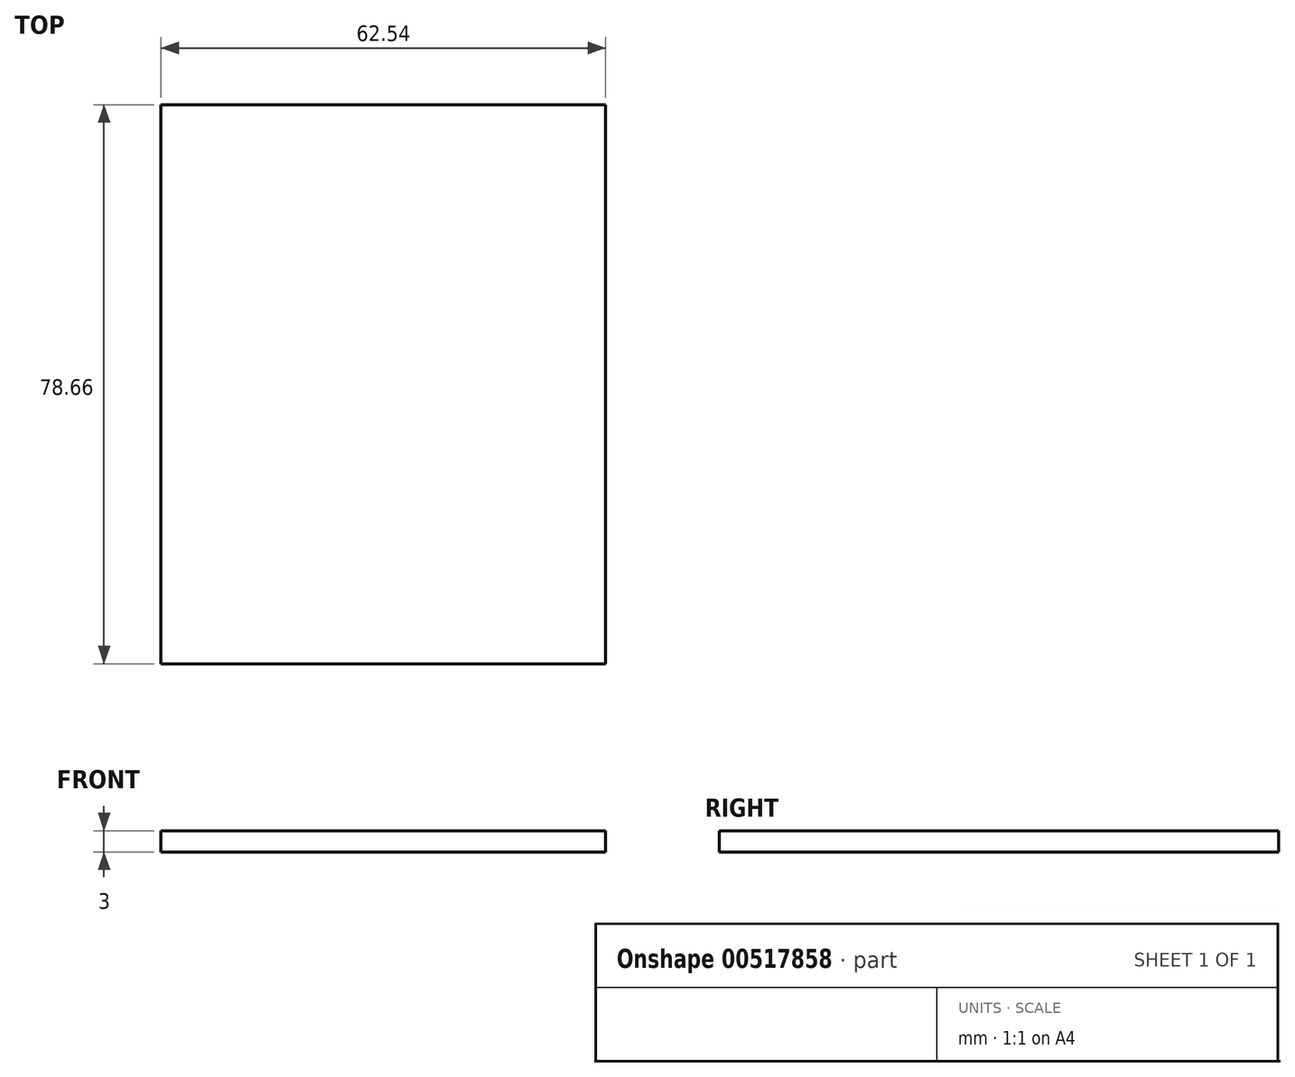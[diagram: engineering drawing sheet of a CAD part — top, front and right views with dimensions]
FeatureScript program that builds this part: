
annotation { "Feature Type Name" : "Feature", "Feature Type Description" : "" }
export const myFeature = defineFeature(function(context is Context, id is Id, definition is map)
    precondition{}
    {
        {
            var Q0;
            Q0=qCreatedBy(makeId("Top.planeOp"),FACE);
            var sketch = newSketch(context, id + "F0", { "sketchPlane" : qUnion([Q0])});
            skLineSegment(sketch, "E0.bottom", {"start": v(31.27, 39.33) * mm, "end": v(-31.27, 39.33) * mm});
            skLineSegment(sketch, "E0.top", {"start": v(31.27, -39.33) * mm, "end": v(-31.27, -39.33) * mm});
            skLineSegment(sketch, "E0.left", {"start": v(31.27, 39.33) * mm, "end": v(31.27, -39.33) * mm});
            skLineSegment(sketch, "E0.right", {"start": v(-31.27, 39.33) * mm, "end": v(-31.27, -39.33) * mm});
            skPoint(sketch, "E0.middle", {"position": v(0, 0) * mm});
            skSolve(sketch);
        }
        {
            var Q0;
            Q0=makeQuery(id+"F0.imprint","IMPRINT",FACE,{"disambiguationData":[TD([[makeQuery(id+"F0.imprint","IMPRINT",EDGE,{"derivedFrom":sQuery(id+"F0.wireOp",EDGE,"E0.bottom")}),1.0]])]});
            extrude(context, id + "F1", {"entities" : qUnion([Q0]), "depth" : 3 * mm, "offsetDistance" : 25 * mm});
        }
    });
